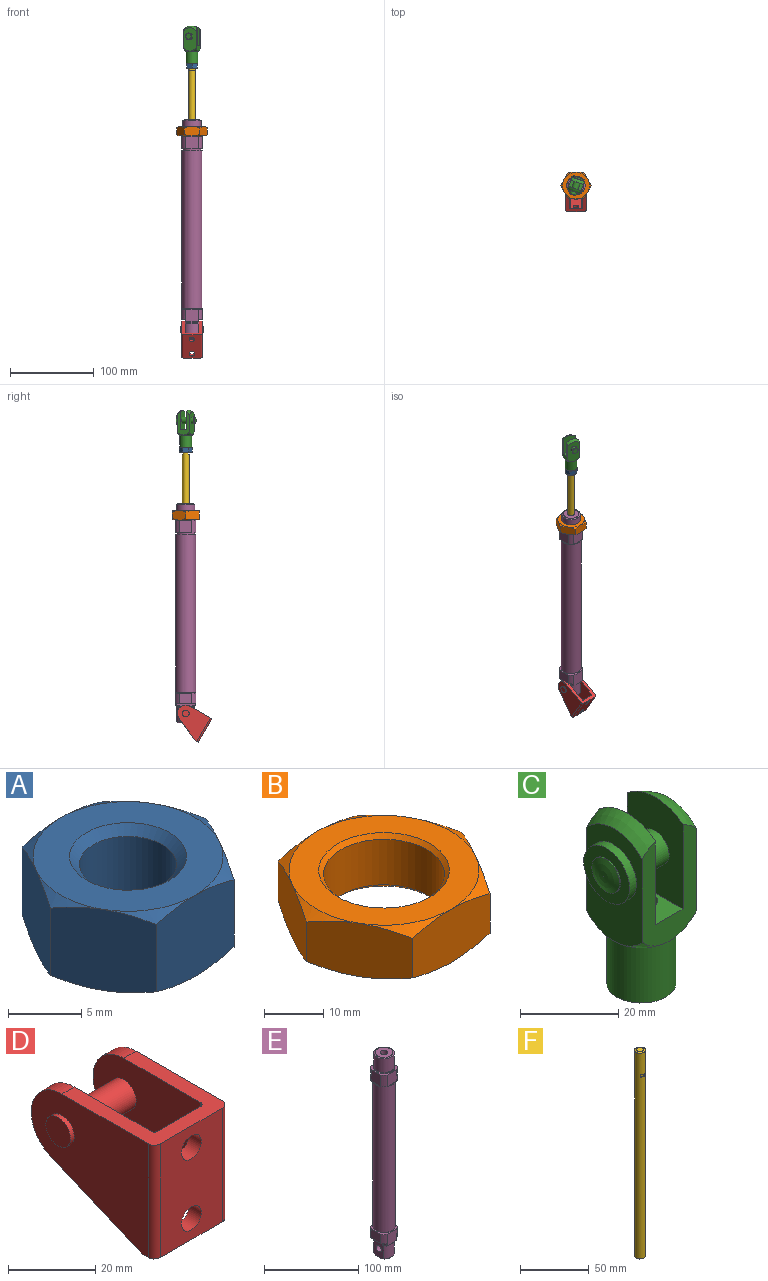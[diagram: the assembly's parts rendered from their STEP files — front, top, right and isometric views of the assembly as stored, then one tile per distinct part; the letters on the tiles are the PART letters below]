
ASSEMBLY  parts=6 mates=10
PART A: 23 faces, bbox 15x15x6.8 mm
  f0: cone r=3.66mm half-angle=45deg, axis (0,0,-1), area 22mm2, adj f1,f16
  f1: cylinder r=3.32mm len=6.65mm, axis (0,0,1), area 113.7mm2, adj f0,f2
  f2: cone r=3.66mm half-angle=45deg, axis (0,0,1), area 22mm2, adj f1,f15
  f3: cone r=7mm half-angle=60deg, axis (0,0,-1), area 2.6mm2, adj f15,f19,f22
  f4: cone r=7mm half-angle=60deg, axis (0,0,-1), area 2.6mm2, adj f15,f17,f20
  f5: cone r=7mm half-angle=60deg, axis (0,0,1), area 2.6mm2, adj f16,f19,f22
  f6: cone r=7mm half-angle=60deg, axis (0,0,1), area 2.6mm2, adj f16,f17,f20
  f7: cone r=7mm half-angle=60deg, axis (0,0,1), area 2.6mm2, adj f16,f18,f19
  f8: cone r=7mm half-angle=60deg, axis (0,0,1), area 2.6mm2, adj f16,f17,f18
  f9: cone r=7mm half-angle=60deg, axis (0,0,1), area 2.6mm2, adj f16,f20,f21
  f10: cone r=7mm half-angle=60deg, axis (0,0,1), area 2.6mm2, adj f16,f21,f22
  f11: cone r=7mm half-angle=60deg, axis (0,0,-1), area 2.6mm2, adj f15,f20,f21
  f12: cone r=7mm half-angle=60deg, axis (0,0,-1), area 2.6mm2, adj f15,f17,f18
  f13: cone r=7mm half-angle=60deg, axis (0,0,-1), area 2.6mm2, adj f15,f18,f19
  f14: cone r=7mm half-angle=60deg, axis (0,0,-1), area 2.6mm2, adj f15,f21,f22
  f15: plane 13x13mm, normal (0,0,1), area 82.5mm2, adj f2,f3,f4,f11,f12,f13,f14
  f16: plane 13x13mm, normal (0,0,-1), area 82.5mm2, adj f0,f5,f6,f7,f8,f9,f10
  f17: plane 6.8x6.51mm, normal (-0.87,-0.5,0), area 48mm2, adj f4,f6,f8,f12,f18,f20
  f18: plane 7.51x6.8mm, normal (0,-1,0), area 48mm2, adj f7,f8,f12,f13,f17,f19
  f19: plane 6.8x6.51mm, normal (0.87,-0.5,0), area 48mm2, adj f3,f5,f7,f13,f18,f22
  f20: plane 6.8x6.51mm, normal (-0.87,0.5,0), area 48mm2, adj f4,f6,f9,f11,f17,f21
  f21: plane 7.51x6.8mm, normal (0,1,0), area 48mm2, adj f9,f10,f11,f14,f20,f22
  f22: plane 6.8x6.51mm, normal (0.87,0.5,0), area 48mm2, adj f3,f5,f10,f14,f19,f21
PART B: 23 faces, bbox 37x37x11 mm
  f0: cone r=10.59mm half-angle=45deg, axis (0,0,-1), area 76.4mm2, adj f1,f16
  f1: cylinder r=10.19mm len=20.38mm, axis (0,0,1), area 600.2mm2, adj f0,f2
  f2: cone r=10.59mm half-angle=45deg, axis (0,0,1), area 76.4mm2, adj f1,f15
  f3: cone r=17.24mm half-angle=60deg, axis (0,0,-1), area 15.9mm2, adj f15,f19,f22
  f4: cone r=17.24mm half-angle=60deg, axis (0,0,-1), area 15.9mm2, adj f15,f17,f20
  f5: cone r=17.24mm half-angle=60deg, axis (0,0,1), area 15.9mm2, adj f16,f19,f22
  f6: cone r=17.24mm half-angle=60deg, axis (0,0,1), area 15.9mm2, adj f16,f17,f20
  f7: cone r=17.24mm half-angle=60deg, axis (0,0,1), area 15.9mm2, adj f16,f18,f19
  f8: cone r=17.24mm half-angle=60deg, axis (0,0,1), area 15.9mm2, adj f16,f17,f18
  f9: cone r=17.24mm half-angle=60deg, axis (0,0,1), area 15.9mm2, adj f16,f20,f21
  f10: cone r=17.24mm half-angle=60deg, axis (0,0,1), area 15.9mm2, adj f16,f21,f22
  f11: cone r=17.24mm half-angle=60deg, axis (0,0,-1), area 15.9mm2, adj f15,f20,f21
  f12: cone r=17.24mm half-angle=60deg, axis (0,0,-1), area 15.9mm2, adj f15,f17,f18
  f13: cone r=17.24mm half-angle=60deg, axis (0,0,-1), area 15.9mm2, adj f15,f18,f19
  f14: cone r=17.24mm half-angle=60deg, axis (0,0,-1), area 15.9mm2, adj f15,f21,f22
  f15: plane 32x32mm, normal (0,0,1), area 424.1mm2, adj f2,f3,f4,f11,f12,f13,f14
  f16: plane 32x32mm, normal (0,0,-1), area 424.1mm2, adj f0,f5,f6,f7,f8,f9,f10
  f17: plane 16.02x11mm, normal (-0.87,-0.5,0), area 185.1mm2, adj f4,f6,f8,f12,f18,f20
  f18: plane 18.49x11mm, normal (0,-1,0), area 185.1mm2, adj f7,f8,f12,f13,f17,f19
  f19: plane 16.02x11mm, normal (0.87,-0.5,0), area 185.1mm2, adj f3,f5,f7,f13,f18,f22
  f20: plane 16.02x11mm, normal (-0.87,0.5,0), area 185.1mm2, adj f4,f6,f9,f11,f17,f21
  f21: plane 18.49x11mm, normal (0,1,0), area 185.1mm2, adj f9,f10,f11,f14,f20,f22
  f22: plane 16.02x11mm, normal (0.87,0.5,0), area 185.1mm2, adj f3,f5,f10,f14,f19,f21
PART C: 24 faces, bbox 23x20x44.4 mm
  f0: sphere r=13mm, area 124.3mm2, adj f1,f19,f21,f22,f23
  f1: cylinder r=7.04mm len=14.08mm, axis (0,0,-1), area 609.2mm2, adj f0,f20
  f2: sphere r=13mm, area 76.4mm2, adj f16,f19,f21,f22
  f3: sphere r=13mm, area 76.4mm2, adj f17,f19,f22,f23
  f4: cone r=3.66mm half-angle=45deg, axis (0,0,-1), area 22mm2, adj f5,f20
  f5: cylinder r=3.32mm len=19.82mm, axis (0,0,-1), area 413.9mm2, adj f4,f18
  f6: cylinder r=4mm len=8mm, axis (1,0,0), area 88.3mm2, adj f10,f21
  f7: sphere r=11mm, area 52mm2, adj f8
  f8: cylinder r=4mm len=8mm, axis (1,0,0), area 6.2mm2, adj f7,f14
  f9: cylinder r=6.6mm len=13.2mm, axis (-1,0,0), area 82.9mm2, adj f13,f14
  f10: cone r=3.66mm half-angle=45deg, axis (-1,0,0), area 22mm2, adj f6,f15
  f11: cylinder r=4mm len=8mm, axis (1,0,0), area 201.1mm2, adj f16,f17
  f12: cylinder r=4mm len=8mm, axis (1,0,0), area 4.8mm2, adj f13,f23
  f13: plane 13.2x13.2mm, normal (1,0,0), area 86.6mm2, adj f9,f12
  f14: plane 13.2x13.2mm, normal (-1,0,0), area 86.6mm2, adj f8,f9
  f15: plane 6.65x6.65mm, normal (1,0,0), area 34.7mm2, adj f10
  f16: plane 23.87x16mm, normal (-1,0,0), area 316.8mm2, adj f2,f11,f18,f19,f22
  f17: plane 23.87x16mm, normal (1,0,0), area 316.8mm2, adj f3,f11,f18,f19,f22
  f18: plane 16x8mm, normal (0,0,1), area 93.3mm2, adj f5,f16,f17,f19,f22
  f19: plane 26.98x15.62mm, normal (0,-1,0), area 227.8mm2, adj f0,f2,f3,f16,f17,f18,f21,f23
  f20: plane 14.08x14.08mm, normal (0,0,-1), area 105.4mm2, adj f1,f4
  f21: plane 28.09x16mm, normal (1,0,0), area 362.4mm2, adj f0,f2,f6,f19,f22
  f22: plane 26.98x15.62mm, normal (0,1,0), area 227.8mm2, adj f0,f2,f3,f16,f17,f18,f21,f23
  f23: plane 28.09x16mm, normal (-1,0,0), area 362.4mm2, adj f0,f3,f12,f19,f22
PART D: 23 faces, bbox 26.5x40x32 mm
  f0: cylinder r=3.25mm len=6.5mm, axis (0,1,0), area 81.7mm2, adj f18,f21
  f1: cylinder r=3.25mm len=6.5mm, axis (0,1,0), area 81.7mm2, adj f18,f21
  f2: cylinder r=4mm len=8mm, axis (-1,0,0), area 30.3mm2, adj f6,f12
  f3: cylinder r=4mm len=16.1mm, axis (-1,0,0), area 404.6mm2, adj f11,f14
  f4: cylinder r=4mm len=8mm, axis (-1,0,0), area 30.3mm2, adj f5,f16
  f5: plane 8x8mm, normal (1,0,0), area 50.3mm2, adj f4
  f6: plane 8x8mm, normal (-1,0,0), area 50.3mm2, adj f2
  f7: plane 29.93x12.81mm, normal (0,0.39,-0.92), area 130.5mm2, adj f9,f13,f14,f16,f22
  f8: plane 29.93x12.81mm, normal (0,0.39,-0.92), area 130.5mm2, adj f10,f11,f12,f19,f22
  f9: cylinder r=10mm len=19.19mm, axis (1,0,0), area 109.5mm2, adj f7,f14,f15,f16
  f10: cylinder r=10mm len=19.19mm, axis (1,0,0), area 109.5mm2, adj f8,f11,f12,f15
  f11: plane 35x31.57mm, normal (1,0,0), area 763.6mm2, adj f3,f8,f10,f15,f19
  f12: plane 38x32mm, normal (-1,0,0), area 859.4mm2, adj f2,f8,f10,f15,f20,f22
  f13: cylinder r=1mm len=32mm, axis (0,0,-1), area 50mm2, adj f7,f14,f15,f18
  f14: plane 35x31.57mm, normal (-1,0,0), area 763.6mm2, adj f3,f7,f9,f13,f15
  f15: plane 30x24.1mm, normal (0,0,1), area 303.1mm2, adj f9,f10,f11,f12,f13,f14,f16,f17
  f16: plane 38x32mm, normal (1,0,0), area 859.4mm2, adj f4,f7,f9,f15,f17,f22
  f17: cylinder r=2mm len=32mm, axis (0,0,-1), area 100.5mm2, adj f15,f16,f21,f22
  f18: plane 32x14.1mm, normal (0,1,0), area 384.8mm2, adj f0,f1,f13,f15,f19,f22
  f19: cylinder r=1mm len=32mm, axis (0,0,-1), area 50mm2, adj f8,f11,f15,f18
  f20: cylinder r=2mm len=32mm, axis (0,0,-1), area 100.5mm2, adj f12,f15,f21,f22
  f21: plane 32x20.1mm, normal (0,-1,0), area 576.8mm2, adj f0,f1,f15,f17,f20,f22
  f22: plane 24.1x4mm, normal (0,0,-1), area 94.7mm2, adj f7,f8,f12,f16,f17,f18,f20,f21
PART E: 61 faces, bbox 24.3x24.3x262.3 mm
  f0: cone r=10.19mm half-angle=63.4deg, axis (0,0,-1), area 116.2mm2, adj f1,f60
  f1: cylinder r=11mm len=22mm, axis (0,0,1), area 1222.5mm2, adj f0,f59
  f2: cylinder r=10.25mm len=20.5mm, axis (0,0,1), area 48.3mm2, adj f58,f59
  f3: cylinder r=11mm len=22mm, axis (0,0,1), area 51.8mm2, adj f49,f58
  f4: cylinder r=10.5mm len=21mm, axis (0,0,-1), area 99mm2, adj f47,f54
  f5: cylinder r=10.5mm len=21mm, axis (0,0,-1), area 99mm2, adj f40,f48
  f6: cylinder r=12mm len=189mm, axis (0,0,-1), area 14250.3mm2, adj f47,f48
  f7: cylinder r=11mm len=16mm, axis (0,0,1), area 13.4mm2, adj f28,f35,f39,f45
  f8: cylinder r=10.25mm len=16mm, axis (0,0,1), area 13.8mm2, adj f28,f35,f38,f39
  f9: cylinder r=11mm len=16.88mm, axis (0,0,1), area 302.3mm2, adj f10,f28,f35,f38
  f10: cone r=10.19mm half-angle=45deg, axis (0,0,1), area 42.8mm2, adj f9,f28,f30,f35
  f11: cylinder r=11mm len=16mm, axis (0,0,1), area 13.4mm2, adj f28,f32,f33,f35
  f12: cylinder r=10.25mm len=16mm, axis (0,0,1), area 13.8mm2, adj f28,f31,f32,f35
  f13: cylinder r=11mm len=16.88mm, axis (0,0,1), area 302.3mm2, adj f14,f28,f31,f35
  f14: cone r=10.19mm half-angle=45deg, axis (0,0,1), area 42.8mm2, adj f13,f28,f30,f35
  f15: cylinder r=4mm len=16mm, axis (-1,0,0), area 402.1mm2, adj f28,f35
  f16: cylinder r=4.28mm len=8.57mm, axis (0,-1,0), area 161.5mm2, adj f25,f27
  f17: cylinder r=4.28mm len=8.57mm, axis (0,-1,0), area 161.5mm2, adj f23,f26
  f18: cylinder r=3.21mm len=12mm, axis (0,-1,0), area 211.7mm2, adj f24,f25,f53
  f19: cylinder r=3.21mm len=12mm, axis (0,-1,0), area 211.7mm2, adj f22,f23,f44
  f20: cylinder r=4mm len=160mm, axis (0,0,-1), area 4021.2mm2, adj f21,f60
  f21: plane 8x8mm, normal (0,0,1), area 50.3mm2, adj f20
  f22: plane 6.42x6.42mm, normal (0,1,0), area 32.4mm2, adj f19
  f23: plane 15x14.42mm, normal (0,1,0), area 150.5mm2, adj f17,f19,f33,f34,f40,f44
  f24: plane 6.42x6.42mm, normal (0,1,0), area 32.4mm2, adj f18
  f25: plane 15x14.42mm, normal (0,1,0), area 150.5mm2, adj f16,f18,f49,f53,f54,f57
  f26: plane 8.57x8.57mm, normal (0,1,0), area 57.6mm2, adj f17
  f27: plane 8.57x8.57mm, normal (0,1,0), area 57.6mm2, adj f16
  f28: plane 23.26x23.24mm, normal (-1,0,0), area 314.8mm2, adj f7,f8,f9,f10,f11,f12,f13,f14
  f29: plane 22.98x4mm, normal (0,0,-1), area 77.2mm2, adj f28,f34,f41,f42
  f30: plane 18.75x16mm, normal (0,0,-1), area 258mm2, adj f10,f14,f28,f35
  f31: plane 16x4.59mm, normal (0,0,1), area 13.6mm2, adj f12,f13,f28,f35
  f32: plane 16x4.59mm, normal (0,0,-1), area 13.6mm2, adj f11,f12,f28,f35
  f33: plane 16x4.45mm, normal (0,0,-1), area 32.7mm2, adj f11,f23,f28,f34,f35,f44
  f34: cylinder r=14mm len=15mm, axis (0,0,-1), area 84.9mm2, adj f23,f28,f29,f33,f40,f41
  f35: plane 23.26x23.24mm, normal (1,0,0), area 314.8mm2, adj f7,f8,f9,f10,f11,f12,f13,f14
  f36: plane 22.98x4mm, normal (0,0,-1), area 77.2mm2, adj f35,f37,f43,f44
  f37: cylinder r=14mm len=15mm, axis (0,0,-1), area 84.9mm2, adj f35,f36,f40,f43,f45,f46
  f38: plane 16x4.59mm, normal (0,0,1), area 13.6mm2, adj f8,f9,f28,f35
  f39: plane 16x4.59mm, normal (0,0,-1), area 13.6mm2, adj f7,f8,f28,f35
  f40: plane 24x24mm, normal (0,0,1), area 191.3mm2, adj f5,f23,f34,f37,f41,f42,f43,f44
  f41: plane 14.42x12mm, normal (-1,0,0), area 173.1mm2, adj f29,f34,f40,f42
  f42: cylinder r=14mm len=15mm, axis (0,0,-1), area 84.9mm2, adj f28,f29,f40,f41,f45,f46
  f43: plane 14.42x12mm, normal (1,0,0), area 173.1mm2, adj f36,f37,f40,f44
  f44: cylinder r=14mm len=15mm, axis (0,0,-1), area 52.1mm2, adj f19,f23,f33,f35,f36,f40,f43
  f45: plane 16x4.45mm, normal (0,0,-1), area 32.7mm2, adj f7,f28,f35,f37,f42,f46
  f46: plane 15x14.42mm, normal (0,-1,0), area 216.3mm2, adj f37,f40,f42,f45
  f47: plane 24x24mm, normal (0,0,1), area 106mm2, adj f4,f6
  f48: plane 24x24mm, normal (0,0,-1), area 106mm2, adj f5,f6
  f49: plane 24x24mm, normal (0,0,1), area 157.5mm2, adj f3,f25,f50,f51,f52,f53,f55,f56
  f50: plane 15x14.42mm, normal (-1,0,0), area 216.3mm2, adj f49,f51,f54,f57
  f51: cylinder r=14mm len=15mm, axis (0,0,-1), area 102.6mm2, adj f49,f50,f54,f56
  f52: plane 15x14.42mm, normal (1,0,0), area 216.3mm2, adj f49,f53,f54,f55
  f53: cylinder r=14mm len=15mm, axis (0,0,-1), area 69.8mm2, adj f18,f25,f49,f52,f54
  f54: plane 24x24mm, normal (0,0,-1), area 191.3mm2, adj f4,f25,f50,f51,f52,f53,f55,f56
  f55: cylinder r=14mm len=15mm, axis (0,0,-1), area 102.6mm2, adj f49,f52,f54,f56
  f56: plane 15x14.42mm, normal (0,-1,0), area 216.3mm2, adj f49,f51,f54,f55
  f57: cylinder r=14mm len=15mm, axis (0,0,-1), area 102.6mm2, adj f25,f49,f50,f54
  f58: plane 22x22mm, normal (0,0,1), area 50.1mm2, adj f2,f3
  f59: plane 22x22mm, normal (0,0,-1), area 50.1mm2, adj f1,f2
  f60: plane 18.75x18.75mm, normal (0,0,1), area 225.9mm2, adj f0,f20
PART F: 10 faces, bbox 8x8x184 mm
  f0: cone r=3.32mm half-angle=63.4deg, axis (0,0,-1), area 31.6mm2, adj f1,f9
  f1: cylinder r=4mm len=183.32mm, axis (0,0,1), area 4584.3mm2, adj f0,f2,f3,f4,f5,f6,f7,f8
  f2: plane 5.29x1mm, normal (0,0,-1), area 3.6mm2, adj f1,f4
  f3: plane 5.29x1mm, normal (0,0,1), area 3.6mm2, adj f1,f4
  f4: plane 5.29x2mm, normal (0,-1,0), area 10.6mm2, adj f1,f2,f3
  f5: plane 5.29x1mm, normal (0,0,1), area 3.6mm2, adj f1,f6
  f6: plane 5.29x2mm, normal (0,1,0), area 10.6mm2, adj f1,f5,f7
  f7: plane 5.29x1mm, normal (0,0,-1), area 3.6mm2, adj f1,f6
  f8: plane 8x8mm, normal (0,0,-1), area 50.3mm2, adj f1
  f9: plane 5.29x5.29mm, normal (0,0,1), area 22mm2, adj f0
PLACE A rot(axis=(0,0,-1),89deg) t=(-271.4,-174.88,114.25)mm
PLACE B t=(-271.4,-174.88,59.58)mm
PLACE C rot(axis=(0,0,-1),110deg) t=(-271.4,-174.88,131.05)mm
PLACE D rot(axis=(1,0,0),30.3deg) t=(-271.45,-205.83,-194.18)mm
PLACE E t=(-271.4,-174.88,63.33)mm fixed
PLACE F t=(-271.4,-174.88,120.25)mm
MATE planar A.f2 <-> F.f2  axis (0,0,-1) through (-271.4,-174.88,124.25)mm
MATE planar E.f35 <-> D.f14  axis (1,0,0) through (-263.4,-174.88,-186.23)mm
MATE cylindrical E.f15 <-> D.f2  axis (1,0,0) through (-263.4,-174.88,-187.67)mm
MATE cylindrical C.f4 <-> F.f0  axis (0,0,-1) through (-271.4,-174.88,131.05)mm
MATE planar C.f4 <-> A.f15  axis (0,0,-1) through (-271.4,-174.88,131.05)mm
MATE slider F.f0 <-> E.f10  axis (0,0,1) through (-271.4,-174.88,144.25)mm
MATE cylindrical F.f0 <-> E.f10  axis (0,0,1) through (-271.4,-174.88,51.91)mm
MATE planar E.f10 <-> B.f3  axis (0,0,1) through (-271.4,-174.88,44.08)mm
MATE cylindrical A.f0 <-> F.f0  axis (0,0,1) through (-271.4,-174.88,131.05)mm
MATE cylindrical B.f0 <-> E.f10  axis (0,0,1) through (-271.4,-174.88,44.89)mm
